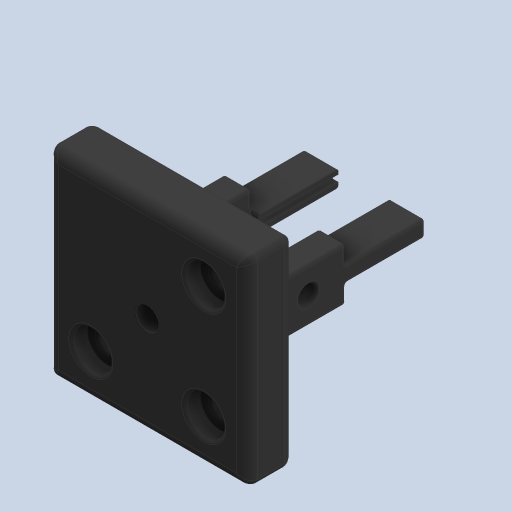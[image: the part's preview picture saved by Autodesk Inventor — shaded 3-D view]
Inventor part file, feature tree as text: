
AUTODESK INVENTOR PART (.ipt)
format: ipt  version: 2023 (Build 270158000, 158)  size: 981,504 bytes
history: native  units: mm
features: other x13, extrude x13, fillet x6, chamfer x4, sketch x3, mirror x1, projected_geometry x1
ambient origin geometry x8: Origin, YZ Plane, XZ Plane, XY Plane, X Axis, Y Axis, Z Axis, Center Point
bodies: Solid1 (feature_tree)
feature tree (41):
  other  "NP1_Payload.ipt"
  other  "Universal_ConstructorHead.ipt"
  other  "Sk:SideArmSlot"
  extrude  "Ex:SideArmSlot"  Depth=10.0mm TaperAngle=0.0deg
  extrude  "Ex:SideArmExtension"  TaperAngle=0.0deg  [1 undecoded]
  other  "Sk:LateralFeatures"
  extrude  "Ex:TopConnection"  Depth=1.0mm
  extrude  "Ex:ThreadProtrusion"  Depth=1.0mm
  fillet  "Fillet:Protrusion"  Radius=6.5mm
  fillet  "Fillet:AllOfArm"  Radius=1.0mm
  extrude  "Ex:ScrewHole"  Depth=10.0mm
  extrude  "Ex:InterArmExtend"  Depth=1.0mm TaperAngle=0.0deg
  other  "Move:InterArmExtend"
  mirror  "Mirror1"
  extrude  "Ex:ThreadInsert"  Depth=9.0mm TaperAngle=0.0deg
  chamfer  "Chamfer:ThreadInsertOpt1"  Distance=10.0mm
  chamfer  "Chamfer:ThreadInsertOpt2"  Distance=3.0mm
  fillet  "Fillet:ThroughHoleOpt1"  Radius=6.5mm
  fillet  "Fillet:ThroughHoleOpt2"  Radius=6.5mm
  other  "TopPlane"
  other  "Sk:TopExpansion"
  fillet  "Fillet:TopCorner"  Radius=6.5mm
  extrude  "Ex:MainTopBody"  Depth=1.0mm
  extrude  "Ex:CavitiesForPosts"  Depth=10.0mm
  extrude  "Ex:TopThread1"  TaperAngle=0.0deg  [1 undecoded]
  chamfer  "Chamfer:TopThread1"  Distance=5.0mm
  extrude  "Ex:PostThroughHoles"  Depth=1.0mm TaperAngle=0.0deg
  extrude  "Ex:ScrewRecesses"  Depth=1.0mm
  extrude  "Ex:TopThread2"  TaperAngle=0.0deg  [1 undecoded]
  chamfer  "Chamfer:TopThread2"  Distance=3.0mm
  fillet  "Fillet:Final"  Radius=7.0mm
  other  "TaggingFeature1"
  other  "TaggingFeature2"
  sketch  "Sketch13"  dims[d0=10.0mm d3=15.0mm d4=0.0mm]
  sketch  "Sketch14"  dims[d21=20.0mm d22=0.0mm d51=0.0mm]
  sketch  "Sketch15"  dims[d52=0.0mm d53=3.16mm d54=1.16mm d55=6.5mm d57=1.0mm d65=10.0mm d80=6.0mm d81=0.0mm d82=9.0mm d83=0.0mm d135=10.0mm d136=0.0mm d137=3.0mm d138=0.0mm d140=6.5mm d141=6.5mm d142=6.5mm d147=5.0mm d148=10.0mm d149=0.0mm d150=5.0mm d151=15.0mm d152=0.0mm d154=8.0mm d155=0.0mm d157=3.0mm d158=7.0mm d159=0.0mm d160=3.3mm d161=0.0mm d162=0.0mm d163=5.9mm d164=5.9mm d165=2.95mm d166=2.95mm d167=0.0mm d168=0.0mm d169=4.9mm d170=3.9mm d171=0.5mm d172=4.9mm d173=20.0mm d174=0.0mm d178=0.2mm d179=2.0mm d180=45.0deg d181=0.2mm d182=2.0mm d183=45.0deg d184=4.9mm d185=0.5mm d186=2.0mm d187=0.1mm d188=10.0mm d189=10.0mm d190=2.0mm d191=3.9mm d192=5.0mm d193=0.0mm d194=0.2mm d195=2.0mm d196=45.0deg d197=10.0mm d198=2.0mm d199=1.0mm d200=0.5mm d201=10.0mm d202=10.0mm d203=3.9mm d204=5.0mm d205=0.0mm d206=0.2mm d207=2.0mm d208=45.0deg d209=0.5mm d210=4.9mm d211=0.5mm d212=4.9mm d216=0.25mm d217=0.0mm d218=0.0mm d219=-0.25mm d220=0.0mm d221=0.0mm d5=0.5mm d6=0.872665mm d97=0.5mm d98=0.872665mm d99=0.5mm d100=0.872665mm d112=1.0mm d113=1.0mm d114=6.0mm d115=0.15mm d116=3.4mm d117=0.375mm d118=14.3117mm d119=6.0mm d120=20.594885mm d121=0.0625mm d122=0.75mm d123=0.375mm d124=14.3117mm d125=0.75mm d126=20.594885mm d127=0.0625mm d128=0.75mm d129=0.375mm d139=1.0mm d143=0.25mm d144=0.375mm d145=14.3117mm d146=0.75mm]
  projected_geometry  "Projected Loop6"
  other  "Solid1::NP1_Payload.ipt"
  other  "Srf1"
  other  "Solid1::Universal_ConstructorHead.ipt"
  other  "Srf2"
note: 3 required parameter values undecoded (feature->parameter linkage not recoverable at this tier; creation-order binding heuristic only, values carry confidence <= 0.55)
